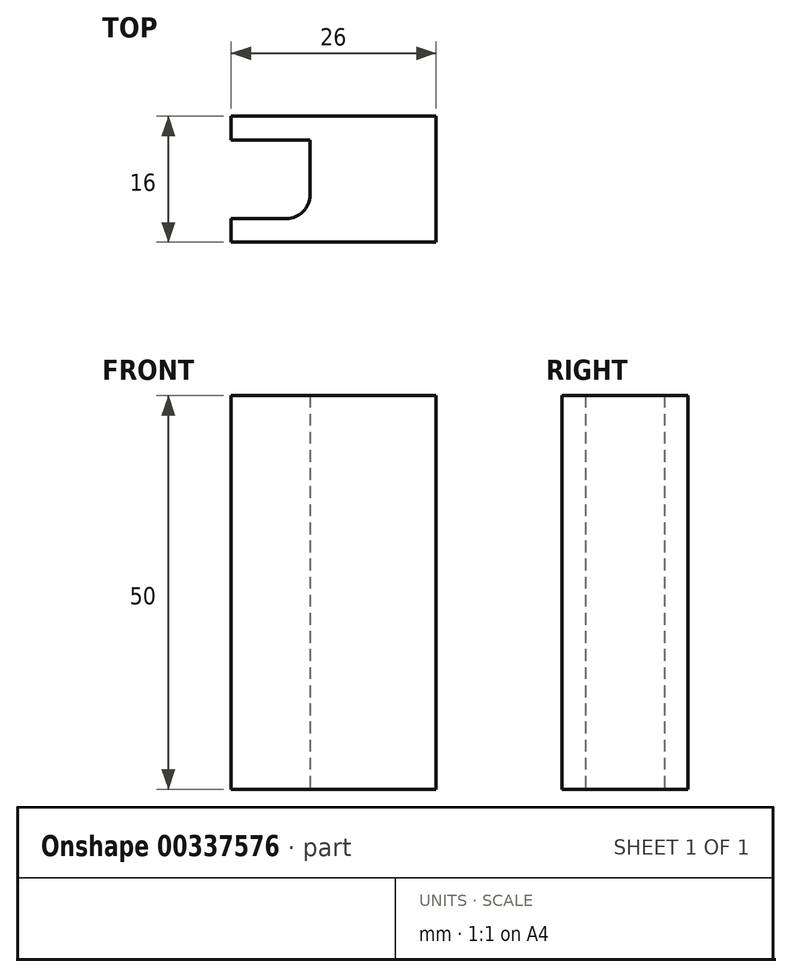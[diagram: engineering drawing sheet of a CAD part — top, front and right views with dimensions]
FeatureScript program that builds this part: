
annotation { "Feature Type Name" : "Feature", "Feature Type Description" : "" }
export const myFeature = defineFeature(function(context is Context, id is Id, definition is map)
    precondition{}
    {
        {
            var Q0;
            Q0=qCreatedBy(makeId("Top.planeOp"),FACE);
            var sketch = newSketch(context, id + "F0", { "sketchPlane" : qUnion([Q0])});
            skLineSegment(sketch, "E0.bottom", {"start": v(0, 0) * mm, "end": v(26, 0) * mm});
            skLineSegment(sketch, "E0.right", {"start": v(26, 0) * mm, "end": v(26, 16) * mm});
            skLineSegment(sketch, "E1", {"start": v(26, 16) * mm, "end": v(0, 16) * mm});
            skLineSegment(sketch, "E2", {"start": v(0, 16) * mm, "end": v(0, 13) * mm});
            skLineSegment(sketch, "E3", {"start": v(0, 13) * mm, "end": v(10, 13) * mm});
            skLineSegment(sketch, "E4", {"start": v(10, 13) * mm, "end": v(10, 6) * mm});
            skLineSegment(sketch, "E5", {"start": v(7, 3) * mm, "end": v(0, 3) * mm});
            skLineSegment(sketch, "E6", {"start": v(0, 3) * mm, "end": v(0, 0) * mm});
            skPoint(sketch, "E7.visualSharp", {"position": v(10, 3) * mm});
            skArc(sketch, "E7.filletArc", {"start": v(7, 3) * mm, "mid": v(9.12, 3.88) * mm, "end": v(10, 6) * mm});
            skSolve(sketch);
        }
        {
            var Q0;
            Q0 = qSketchRegion(id + "F0", true);
            extrude(context, id + "F1", {"entities" : qUnion([Q0]), "depth" : 50 * mm});
        }
    });
